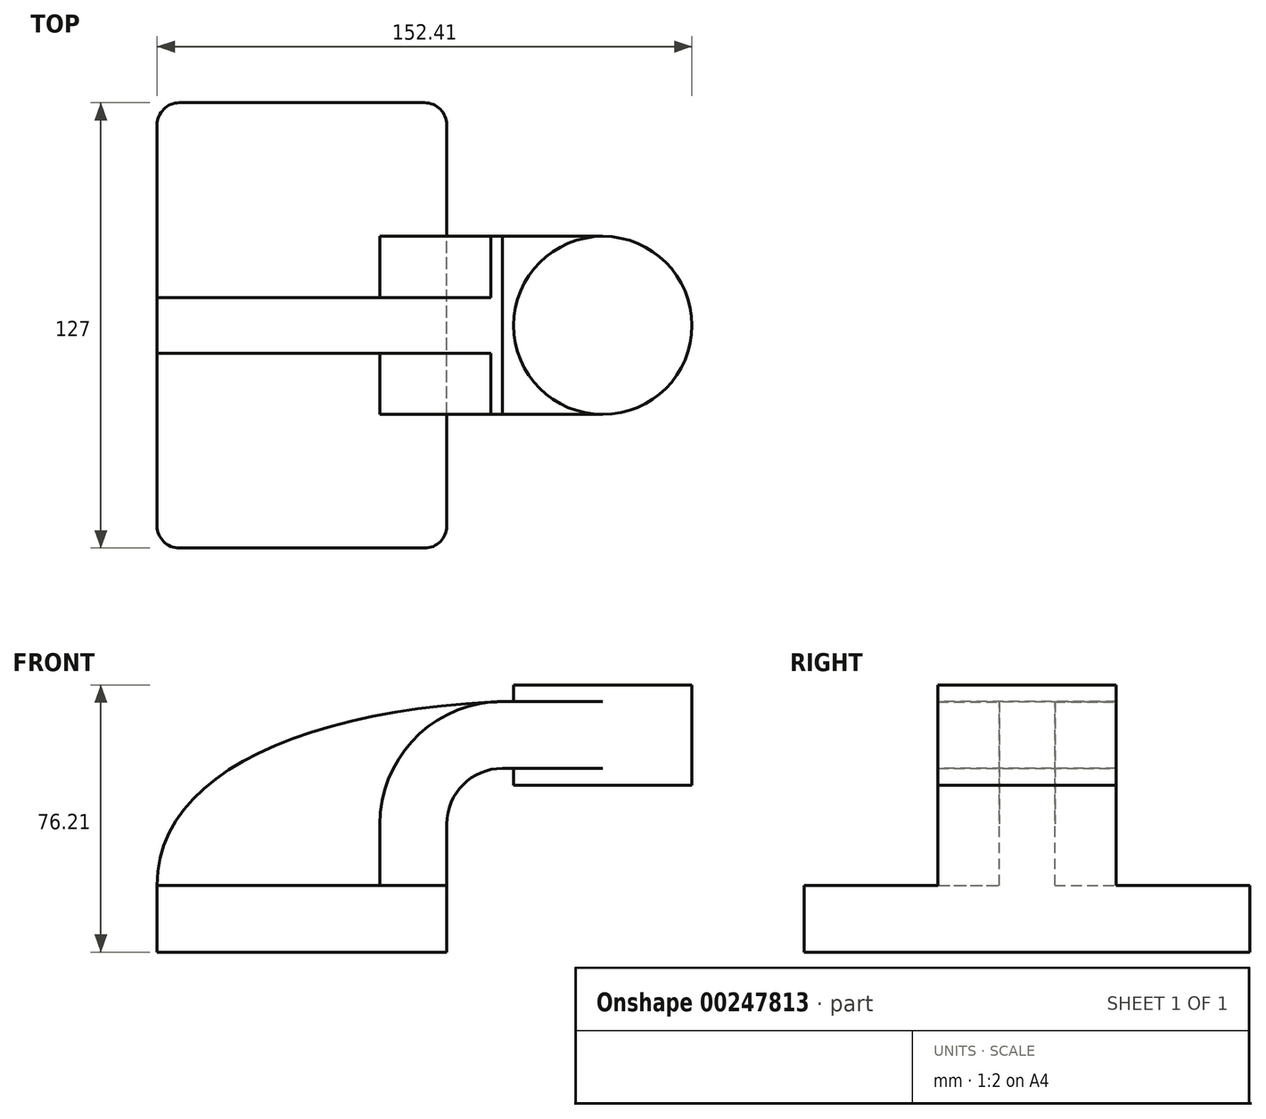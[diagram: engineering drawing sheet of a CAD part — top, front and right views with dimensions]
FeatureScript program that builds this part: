
annotation { "Feature Type Name" : "Feature", "Feature Type Description" : "" }
export const myFeature = defineFeature(function(context is Context, id is Id, definition is map)
    precondition{}
    {
        {
            var Q0;
            Q0=qCreatedBy(makeId("Front.planeOp"),FACE);
            var sketch = newSketch(context, id + "F0", { "sketchPlane" : qUnion([Q0])});
            skLineSegment(sketch, "E0.bottom", {"start": v(-41.28, 9.52) * mm, "end": v(41.28, 9.53) * mm});
            skLineSegment(sketch, "E0.top", {"start": v(-41.27, -9.53) * mm, "end": v(41.28, -9.53) * mm});
            skLineSegment(sketch, "E0.left", {"start": v(-41.28, 9.52) * mm, "end": v(-41.28, -9.53) * mm});
            skLineSegment(sketch, "E0.right", {"start": v(41.28, 9.53) * mm, "end": v(41.28, -9.52) * mm});
            skPoint(sketch, "E0.middle", {"position": v(0, 0) * mm});
            skLineSegment(sketch, "E1.bottom", {"start": v(60.32, 38.1) * mm, "end": v(111.12, 38.1) * mm});
            skLineSegment(sketch, "E1.top", {"start": v(60.32, 66.68) * mm, "end": v(111.12, 66.68) * mm});
            skLineSegment(sketch, "E1.left", {"start": v(60.32, 38.1) * mm, "end": v(60.32, 66.68) * mm});
            skLineSegment(sketch, "E1.right", {"start": v(111.12, 38.1) * mm, "end": v(111.12, 66.68) * mm});
            skPoint(sketch, "E1.middle", {"position": v(85.72, 52.39) * mm});
            skLineSegment(sketch, "E2", {"start": v(41.27, 9.53) * mm, "end": v(41.27, 27) * mm});
            skArc(sketch, "E3", {"start": v(41.27, 27) * mm, "mid": v(45.92, 38.23) * mm, "end": v(57.15, 42.88) * mm});
            skLineSegment(sketch, "E4", {"start": v(57.15, 42.88) * mm, "end": v(85.72, 42.88) * mm});
            skLineSegment(sketch, "E5.0", {"start": v(57.15, 61.93) * mm, "end": v(85.72, 61.93) * mm});
            skArc(sketch, "E5.1", {"start": v(22.22, 27) * mm, "mid": v(32.45, 51.7) * mm, "end": v(57.15, 61.93) * mm});
            skLineSegment(sketch, "E5.2", {"start": v(22.22, 9.53) * mm, "end": v(22.22, 27) * mm});
            skLineSegment(sketch, "E6", {"start": v(85.72, 38.1) * mm, "end": v(85.72, 42.88) * mm});
            skLineSegment(sketch, "E7", {"start": v(85.72, 66.68) * mm, "end": v(85.73, 38.1) * mm});
            skFitSpline(sketch, "E8", {"points": [v(-41.28, 9.52) * mm, v(57.15, 61.93) * mm], "startDerivative": vector(-0.65, 94.3) * mm, "endDerivative": vector(171.45, 7.11) * mm});
            skSolve(sketch);
        }
        {
            var Q0;
            Q0=makeQuery(id+"F0.imprint","IMPRINT",FACE,{"disambiguationData":[TD([[makeQuery(id+"F0.imprint","IMPRINT",EDGE,{"derivedFrom":sQuery(id+"F0.wireOp",EDGE,"E0.top")}),1.0]])]});
            extrude(context, id + "F1", {"entities" : qUnion([Q0]), "endBound" : BoundingType.SYMMETRIC, "depth" : 127 * mm});
        }
        {
            var Q0;
            {var subQ1=sQuery(id+"F0.wireOp",EDGE,"E2");Q0=makeQuery(id+"F0.imprint","IMPRINT",FACE,{"disambiguationData":[TD([[makeQuery(id+"F0.imprint","IMPRINT",EDGE,{"derivedFrom":subQ1}),1.0]])]});}
            var Q1;
            {var subQ0=sQuery(id+"F0.wireOp",EDGE,"E4");var subQ1=sQuery(id+"F0.wireOp",EDGE,"E1.left");var subQ2=makeQuery(id+"F0.imprint","INTERSECT",VERTEX,{"derivedFrom":[subQ1,subQ0]});Q1=makeQuery(id+"F0.imprint","IMPRINT",FACE,{"disambiguationData":[TD([[makeQuery(id+"F0.imprint","IMPRINT",EDGE,{"disambiguationData":[TD([[subQ2,-1.0]])],"derivedFrom":subQ1}),-1.0]])]});}
            extrude(context, id + "F2", {"entities" : qUnion([Q0, Q1]), "operationType" : NewBodyOperationType.ADD, "endBound" : BoundingType.SYMMETRIC, "depth" : 50.8 * mm});
        }
        {
            var Q0;
            {var subQ3=sQuery(id+"F0.wireOp",EDGE,"E5.2");Q0=makeQuery(id+"F0.imprint","IMPRINT",FACE,{"disambiguationData":[TD([[makeQuery(id+"F0.imprint","IMPRINT",EDGE,{"derivedFrom":subQ3}),1.0]])]});}
            extrude(context, id + "F3", {"entities" : qUnion([Q0]), "operationType" : NewBodyOperationType.ADD, "endBound" : BoundingType.SYMMETRIC, "depth" : 15.88 * mm});
        }
        {
            var Q0;
            {var subQ0=sQuery(id+"F0.wireOp",EDGE,"E1.right");Q0=makeQuery(id+"F0.imprint","IMPRINT",FACE,{"disambiguationData":[TD([[makeQuery(id+"F0.imprint","IMPRINT",EDGE,{"derivedFrom":subQ0}),1.0]])]});}
            var Q1;
            Q1=sQuery(id+"F0.wireOp",EDGE,"E7");
            revolve(context, id + "F4", {"operationType" : NewBodyOperationType.ADD, "entities" : qUnion([Q0]), "axis" : qUnion([Q1]), "revolveType" : RevolveType.FULL});
        }
        {
            var Q0;
            Q0=makeQuery(id+"F1.opExtrude","CAP_EDGE",EDGE,{"disambiguationData":[OSD([sQuery(id+"F0.wireOp",EDGE,"E0.left")])],"isStart":false});
            var Q1;
            Q1=makeQuery(id+"F1.opExtrude","CAP_EDGE",EDGE,{"disambiguationData":[OSD([sQuery(id+"F0.wireOp",EDGE,"E0.right")])],"isStart":false});
            var Q2;
            Q2=makeQuery(id+"F1.opExtrude","CAP_EDGE",EDGE,{"disambiguationData":[OSD([sQuery(id+"F0.wireOp",EDGE,"E0.right")])],"isStart":true});
            var Q3;
            Q3=makeQuery(id+"F1.opExtrude","CAP_EDGE",EDGE,{"disambiguationData":[OSD([sQuery(id+"F0.wireOp",EDGE,"E0.left")])],"isStart":true});
            fillet(context, id + "F5", {"entities" : qUnion([Q0, Q1, Q2, Q3]), "radius" : 6.35 * mm, "tangentPropagation" : true, "allowEdgeOverflow" : false});
        }
    });
